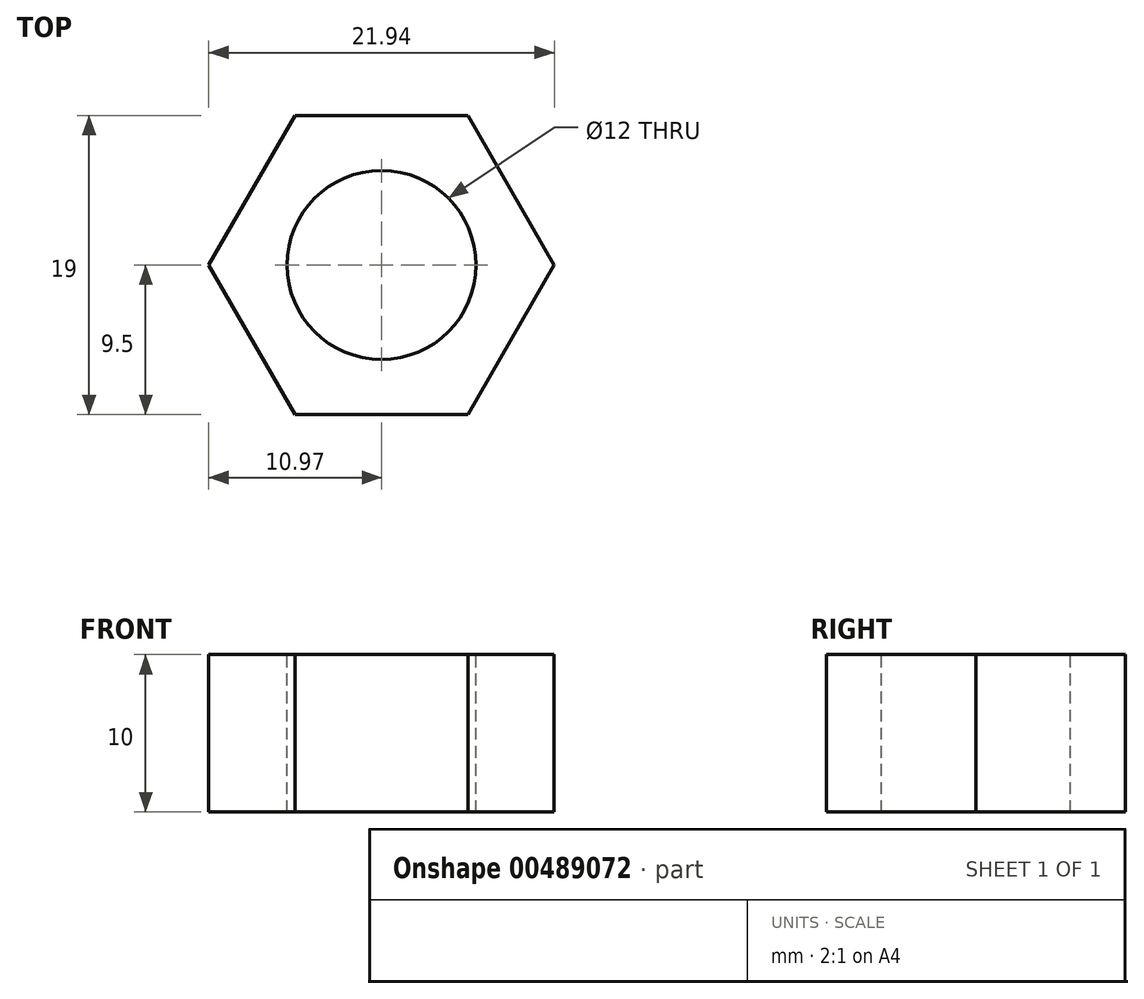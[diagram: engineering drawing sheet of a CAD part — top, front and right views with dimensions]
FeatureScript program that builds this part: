
annotation { "Feature Type Name" : "Feature", "Feature Type Description" : "" }
export const myFeature = defineFeature(function(context is Context, id is Id, definition is map)
    precondition{}
    {
        {
            var Q0;
            Q0=qCreatedBy(makeId("Top.planeOp"),FACE);
            var sketch = newSketch(context, id + "F0", { "sketchPlane" : qUnion([Q0])});
            skCircle(sketch, "E0", {"center": v(0, 0) * mm, "radius": 9.5 * mm, "construction": true});
            skLineSegment(sketch, "E1", {"start": v(5.48, 9.5) * mm, "end": v(10.97, 0) * mm});
            skLineSegment(sketch, "E2", {"start": v(-10.97, 0) * mm, "end": v(-5.48, 9.5) * mm});
            skLineSegment(sketch, "E3", {"start": v(-5.48, 9.5) * mm, "end": v(5.48, 9.5) * mm});
            skLineSegment(sketch, "E4.1.0", {"start": v(10.97, 0) * mm, "end": v(5.48, -9.5) * mm});
            skLineSegment(sketch, "E4.1.1", {"start": v(5.48, -9.5) * mm, "end": v(-5.48, -9.5) * mm});
            skLineSegment(sketch, "E4.1.2", {"start": v(-5.48, -9.5) * mm, "end": v(-10.97, 0) * mm});
            skSolve(sketch);
        }
        {
            var Q0;
            Q0=makeQuery(id+"F0.imprint","IMPRINT",FACE,{"disambiguationData":[TD([[makeQuery(id+"F0.imprint","IMPRINT",EDGE,{"derivedFrom":sQuery(id+"F0.wireOp",EDGE,"E1")}),-1.0]])]});
            extrude(context, id + "F1", {"entities" : qUnion([Q0]), "depth" : 10 * mm});
        }
        {
            var Q0;
            Q0=makeQuery(id+"F1.opExtrude","CAP_FACE",FACE,{"disambiguationData":[OSD([sQuery(id+"F0.wireOp",EDGE,"E1"),sQuery(id+"F0.wireOp",EDGE,"E2"),sQuery(id+"F0.wireOp",EDGE,"E3"),sQuery(id+"F0.wireOp",EDGE,"E4.1.0"),sQuery(id+"F0.wireOp",EDGE,"E4.1.1"),sQuery(id+"F0.wireOp",EDGE,"E4.1.2")])],"isStart":false});
            var sketch = newSketch(context, id + "F2", { "sketchPlane" : qUnion([Q0])});
            skCircle(sketch, "E5", {"center": v(0, 0) * mm, "radius": 6 * mm});
            skSolve(sketch);
        }
        {
            var Q0;
            Q0 = qSketchRegion(id + "F2", true);
            extrude(context, id + "F3", {"entities" : qUnion([Q0]), "operationType" : NewBodyOperationType.REMOVE, "oppositeDirection" : true, "depth" : 25 * mm});
        }
    });
